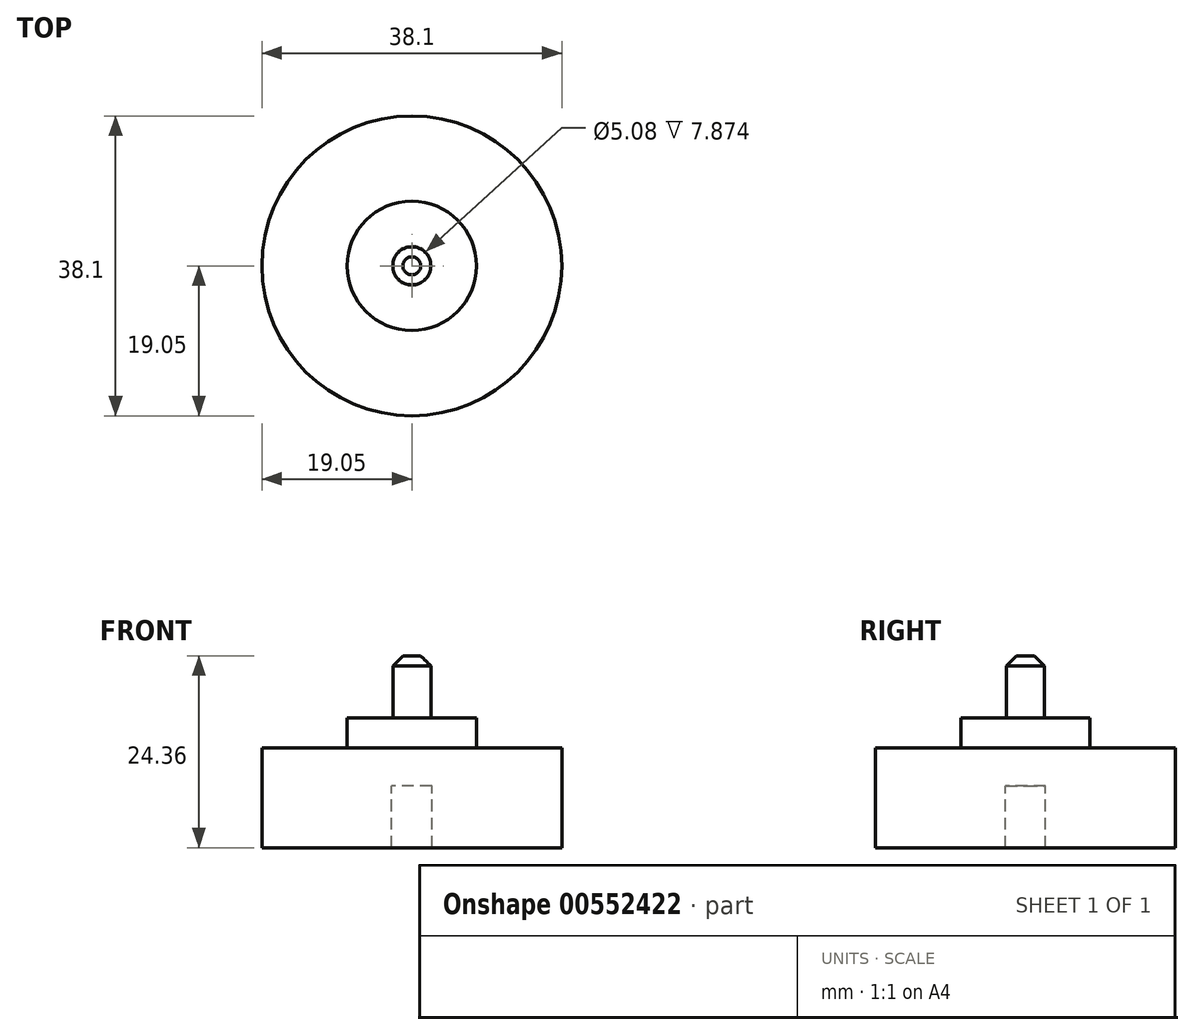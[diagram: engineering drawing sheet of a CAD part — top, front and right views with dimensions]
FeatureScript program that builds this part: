
annotation { "Feature Type Name" : "Feature", "Feature Type Description" : "" }
export const myFeature = defineFeature(function(context is Context, id is Id, definition is map)
    precondition{}
    {
        {
            var Q0;
            Q0=qCreatedBy(makeId("Front.planeOp"),FACE);
            var sketch = newSketch(context, id + "F0", { "sketchPlane" : qUnion([Q0])});
            skLineSegment(sketch, "E0", {"start": v(19.05, 0) * mm, "end": v(19.05, 12.7) * mm});
            skLineSegment(sketch, "E1", {"start": v(19.05, 12.7) * mm, "end": v(8.15, 12.7) * mm});
            skLineSegment(sketch, "E2", {"start": v(2.54, 0) * mm, "end": v(2.54, 7.87) * mm});
            skLineSegment(sketch, "E3", {"start": v(2.54, 7.87) * mm, "end": v(0, 7.87) * mm});
            skLineSegment(sketch, "E4", {"start": v(2.54, 0) * mm, "end": v(19.05, 0) * mm});
            skPoint(sketch, "E5.start.orphan", {"position": v(0, 12.7) * mm});
            skLineSegment(sketch, "E6", {"start": v(2.41, 16.51) * mm, "end": v(8.2, 16.51) * mm});
            skLineSegment(sketch, "E7", {"start": v(8.2, 16.51) * mm, "end": v(8.2, 12.7) * mm});
            skLineSegment(sketch, "E8", {"start": v(0, 24.36) * mm, "end": v(2.41, 24.36) * mm});
            skLineSegment(sketch, "E9", {"start": v(2.41, 24.36) * mm, "end": v(2.41, 16.51) * mm});
            skPoint(sketch, "E10.start.orphan", {"position": v(0, 16.51) * mm});
            skLineSegment(sketch, "E11", {"start": v(0, 24.36) * mm, "end": v(0, 7.87) * mm});
            skSolve(sketch);
        }
        {
            var Q0;
            Q0 = qSketchRegion(id + "F0", true);
            var Q1;
            Q1=sQuery(id+"F0.wireOp",EDGE,"E11");
            revolve(context, id + "F1", {"entities" : qUnion([Q0]), "axis" : qUnion([Q1]), "revolveType" : RevolveType.FULL});
        }
        {
            var Q0;
            Q0=makeQuery(id+"F1.opRevolve","SWEPT_EDGE",EDGE,{"disambiguationData":[OSD([sQuery(id+"F0.wireOp",EDGE,"E8"),sQuery(id+"F0.wireOp",EDGE,"E9")])]});
            chamfer(context, id + "F2", {"entities" : qUnion([Q0]), "width" : 1.27 * mm, "tangentPropagation" : true});
        }
    });
